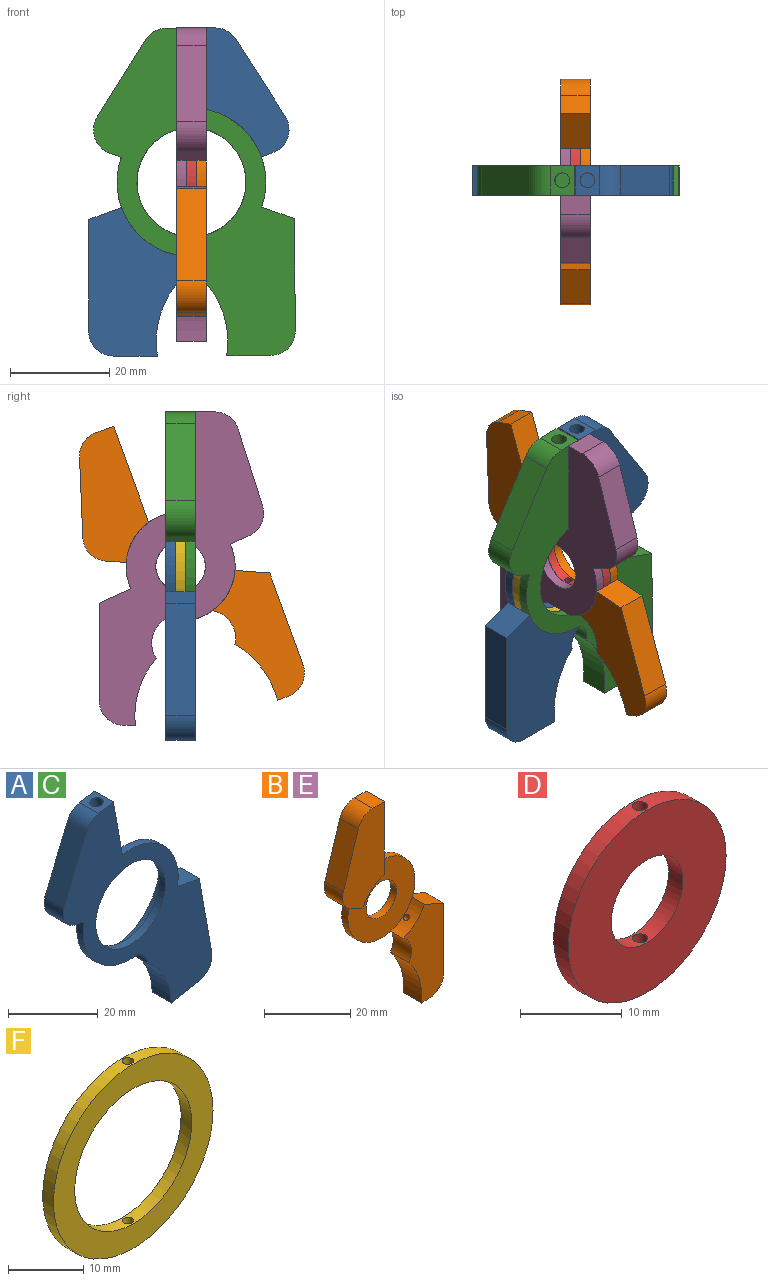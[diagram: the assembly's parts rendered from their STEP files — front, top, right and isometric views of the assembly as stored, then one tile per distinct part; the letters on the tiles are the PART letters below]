
ASSEMBLY  parts=6 mates=5
PART A: 27 faces, bbox 47x6x64 mm
  f0: cylinder r=15mm len=12.17mm, axis (0,1,0), area 71.5mm2, adj f1,f6,f9,f16,f23
  f1: plane 28.05x18.69mm, normal (0,1,0), area 285mm2, adj f0,f6,f7,f8,f9,f19,f20
  f2: plane 8.74x6mm, normal (0.17,0,-0.98), area 53.2mm2, adj f12,f13,f14,f18
  f3: plane 22.22x6mm, normal (0.98,0,0.17), area 135.4mm2, adj f4,f13,f14,f18
  f4: plane 6.9x6mm, normal (0.17,0,0.98), area 42.1mm2, adj f3,f5,f13,f14,f15
  f5: cylinder r=15mm len=17.6mm, axis (0,1,0), area 57.6mm2, adj f4,f6,f13,f16
  f6: plane 15.88x6mm, normal (0.98,0,0.17), area 96.7mm2, adj f0,f1,f5,f7,f13
  f7: plane 6x4.69mm, normal (-0.17,0,0.98), area 21.5mm2, adj f1,f6,f13,f19,f21
  f8: plane 16.95x7.07mm, normal (-0.92,0,0.38), area 110.2mm2, adj f1,f13,f19,f20
  f9: plane 6x2.39mm, normal (-0.17,0,-0.98), area 14.6mm2, adj f0,f1,f10,f13,f20
  f10: cylinder r=15mm len=17.6mm, axis (0,1,0), area 57.6mm2, adj f9,f11,f13,f16
  f11: cylinder r=3.91mm len=6mm, axis (0,1,0), area 30.8mm2, adj f10,f12,f13,f14,f15
  f12: cylinder r=18.23mm len=14.62mm, axis (0,1,0), area 102.5mm2, adj f2,f11,f13,f14
  f13: plane 64.02x46.96mm, normal (0,-1,0), area 1019.7mm2, adj f2,f3,f4,f5,f6,f7,f8,f9
  f14: plane 30.77x23.06mm, normal (0,1,0), area 408mm2, adj f2,f3,f4,f11,f12,f15,f18
  f15: cylinder r=15mm len=12.17mm, axis (0,1,0), area 71.5mm2, adj f4,f11,f14,f16,f25
  f16: plane 30x30mm, normal (0,1,0), area 326.7mm2, adj f0,f5,f10,f15,f17
  f17: cylinder r=11mm len=22mm, axis (0,1,0), area 138.2mm2, adj f13,f16
  f18: cylinder r=5mm len=6mm, axis (0,1,0), area 47.1mm2, adj f2,f3,f13,f14
  f19: cylinder r=5mm len=6mm, axis (0,1,0), area 30mm2, adj f1,f7,f8,f13
  f20: cylinder r=5mm len=6.85mm, axis (0,1,0), area 53.7mm2, adj f1,f8,f9,f13
  f21: cylinder r=1.5mm len=10.37mm, axis (-0.17,0,0.98), area 94.2mm2, adj f7,f22
  f22: plane 3x2.95mm, normal (-0.17,0,0.98), area 7.1mm2, adj f21
  f23: cylinder r=0.75mm len=2.69mm, axis (0.71,0,-0.71), area 10.8mm2, adj f0,f24
  f24: plane 1.5x1.06mm, normal (0.71,0,-0.71), area 1.8mm2, adj f23
  f25: cylinder r=0.75mm len=2.69mm, axis (-0.71,0,0.71), area 10.8mm2, adj f15,f26
  f26: plane 1.5x1.06mm, normal (-0.71,0,0.71), area 1.8mm2, adj f25
PART B: 25 faces, bbox 33.2x6x63.2 mm
  f0: cylinder r=11mm len=7.04mm, axis (0,-1,0), area 36.6mm2, adj f6,f11,f13,f16,f21
  f1: plane 26.68x13.76mm, normal (0,-1,0), area 263.2mm2, adj f7,f8,f9,f10,f15,f18,f19
  f2: cylinder r=11mm len=15.5mm, axis (0,1,0), area 49.9mm2, adj f6,f7,f14,f16
  f3: cylinder r=11mm len=15.5mm, axis (0,1,0), area 49.9mm2, adj f10,f11,f14,f16
  f4: plane 6x2.28mm, normal (0,0,-1), area 13.7mm2, adj f12,f13,f14,f17
  f5: plane 19.65x6mm, normal (1,0,0), area 117.9mm2, adj f6,f13,f14,f17
  f6: plane 6.4x6mm, normal (0.41,0,0.91), area 42.1mm2, adj f0,f2,f5,f13,f14
  f7: plane 20.6x6mm, normal (1,0,0), area 123.6mm2, adj f1,f2,f8,f14,f15
  f8: plane 6x3.84mm, normal (0,0,1), area 23.1mm2, adj f1,f7,f14,f18
  f9: plane 15.43x6mm, normal (-0.95,0,0.3), area 97.1mm2, adj f1,f14,f18,f19
  f10: plane 6x3.77mm, normal (-0.41,0,-0.91), area 24.8mm2, adj f1,f3,f14,f15,f19
  f11: cylinder r=5.6mm len=7.92mm, axis (0,1,0), area 54.8mm2, adj f0,f3,f12,f13,f14
  f12: cylinder r=18.23mm len=13.52mm, axis (0,1,0), area 87.3mm2, adj f4,f11,f13,f14
  f13: plane 27.52x13.43mm, normal (0,-1,0), area 241.4mm2, adj f0,f4,f5,f6,f11,f12,f17
  f14: plane 63.21x33.19mm, normal (0,1,0), area 806.2mm2, adj f2,f3,f4,f5,f6,f7,f8,f9
  f15: cylinder r=11mm len=7.04mm, axis (0,-1,0), area 36.6mm2, adj f1,f7,f10,f16,f23
  f16: plane 22x22mm, normal (0,-1,0), area 301.6mm2, adj f0,f2,f3,f15,f20
  f17: cylinder r=5mm len=6mm, axis (0,1,0), area 47.1mm2, adj f4,f5,f13,f14
  f18: cylinder r=5mm len=6mm, axis (0,1,0), area 37.9mm2, adj f1,f8,f9,f14
  f19: cylinder r=5mm len=6.08mm, axis (0,1,0), area 43.7mm2, adj f1,f9,f10,f14
  f20: cylinder r=5mm len=10mm, axis (0,1,0), area 62.8mm2, adj f14,f16
  f21: cylinder r=0.75mm len=2.49mm, axis (-0.65,0,0.76), area 9.3mm2, adj f0,f22
  f22: plane 1.5x1.14mm, normal (-0.65,0,0.76), area 1.8mm2, adj f21
  f23: cylinder r=0.75mm len=2.49mm, axis (0.65,0,-0.76), area 9.3mm2, adj f15,f24
  f24: plane 1.5x1.14mm, normal (0.65,0,-0.76), area 1.8mm2, adj f23
PART C: same geometry as A
PART D: 6 faces, bbox 22x2x22 mm
  f0: cylinder r=11mm len=22mm, axis (0,1,0), area 134.7mm2, adj f2,f3,f4,f5
  f1: cylinder r=5mm len=10mm, axis (0,1,0), area 59.3mm2, adj f2,f3,f4,f5
  f2: plane 22x22mm, normal (0,-1,0), area 301.6mm2, adj f0,f1
  f3: plane 22x22mm, normal (0,1,0), area 301.6mm2, adj f0,f1
  f4: cylinder r=0.75mm len=6.06mm, axis (0,0,-1), area 28.3mm2, adj f0,f1
  f5: cylinder r=0.75mm len=6.06mm, axis (0,0,-1), area 28.3mm2, adj f0,f1
PART E: same geometry as B
PART F: 6 faces, bbox 30x2x30 mm
  f0: cylinder r=15mm len=30mm, axis (0,1,0), area 185mm2, adj f2,f3,f4,f5
  f1: cylinder r=11mm len=22mm, axis (0,-1,0), area 134.7mm2, adj f2,f3,f4,f5
  f2: plane 30x30mm, normal (0,-1,0), area 326.7mm2, adj f0,f1
  f3: plane 30x30mm, normal (0,1,0), area 326.7mm2, adj f0,f1
  f4: cylinder r=0.75mm len=4.03mm, axis (0,0,-1), area 18.9mm2, adj f0,f1
  f5: cylinder r=0.75mm len=4.03mm, axis (0,0,-1), area 18.9mm2, adj f0,f1
PLACE A rot(axis=(-0.09,0,1),180deg) t=(0,-2,0)mm
PLACE B rot(axis=(-0.17,-0.17,-0.97),91.7deg) t=(3,1,-0.05)mm
PLACE C rot(axis=(0,1,0),9.5deg) t=(0,4,0)mm
PLACE D rot(axis=(0,0,-1),90deg) t=(1,65.23,-20.33)mm
PLACE E rot(axis=(0,0,1),90deg) t=(-3,1,-0.05)mm
PLACE F t=(-36.59,2,-37.93)mm
MATE fastened D.f4 <-> F.f4  axis (0,0,1) through (0,1,10.95)mm
MATE revolute C.f0 <-> F.f0  axis (0,1,0) through (0,0,0)mm
MATE revolute B.f20 <-> D.f0  axis (-1,0,0) through (1,1,-0.05)mm
MATE revolute E.f20 <-> D.f0  axis (1,0,0) through (-1,1,-0.05)mm
MATE revolute A.f0 <-> F.f0  axis (0,-1,0) through (0,2,0)mm
